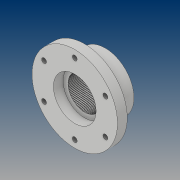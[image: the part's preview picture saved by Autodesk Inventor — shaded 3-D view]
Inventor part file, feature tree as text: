
AUTODESK INVENTOR PART (.ipt)
format: ipt  version: 2021 (Build 250183000, 183)  size: 785,408 bytes
history: native  units: mm
features: thread x6, extrude x3, sketch x3, other x2, pattern_circular x1
ambient origin geometry x8: Origin, YZ Plane, XZ Plane, XY Plane, X Axis, Y Axis, Z Axis, Center Point
bodies: Solid1 (feature_tree)
feature tree (15):
  extrude  "Extrusion1"  Depth=235.0mm
  other  "Involute Splining1"
  extrude  "Extrusion2"  Depth=175.0mm
  extrude  "Extrusion3"  Depth=40.0mm TaperAngle=0.0deg
  pattern_circular  "Circular Pattern1"  Count=2  [1 undecoded]
  thread  "Thread1"  [1 undecoded]
  thread  "Thread2"  [1 undecoded]
  thread  "Thread3"  [1 undecoded]
  thread  "Thread4"  [1 undecoded]
  thread  "Thread5"  [1 undecoded]
  thread  "Thread6"  [1 undecoded]
  sketch  "Sketch1"  dims[d0=135.0mm d1=235.0mm]
  other  "Hub Groove"
  sketch  "Sketch3"  dims[d2=85.0mm d3=0.0mm d6=175.0mm]
  sketch  "Sketch4"  dims[d7=350.0mm d8=40.0mm d9=0.0mm d10=20.0mm d11=145.0mm d12=50.0mm d13=0.0mm d14=60.0mm d15=360.0deg d17=10.0mm d18=0.0mm d19=10.0mm d20=0.0mm d21=10.0mm d22=0.0mm d23=10.0mm d24=0.0mm d25=40.0mm d26=0.0mm d27=40.0mm d28=0.0mm]
note: 7 required parameter values undecoded (feature->parameter linkage not recoverable at this tier; creation-order binding heuristic only, values carry confidence <= 0.55)
